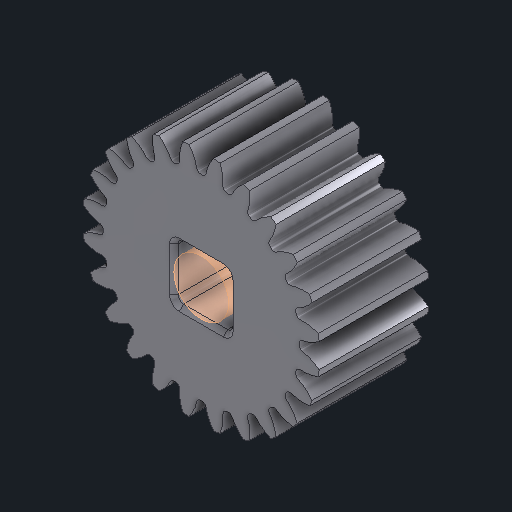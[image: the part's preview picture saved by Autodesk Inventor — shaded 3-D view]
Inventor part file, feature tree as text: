
AUTODESK INVENTOR PART (.ipt)
format: ipt  version: 2025 (Build 290162000, 162)  size: 466,944 bytes
history: native  units: in
note: dims shown in document units (in); Inventor stores cm internally (conversion verified against a paired STEP export)
features: other x5, sketch x1
ambient origin geometry x8: Origin, YZ Plane, XZ Plane, XY Plane, X Axis, Y Axis, Z Axis, Center Point
bodies: Solid1 (feature_tree)
feature tree (6):
  other  "HS 24T Gear, No Insert.ipt"
  other  "Solid1::HS 24T Gear, No Insert.ipt"
  other  "TaggingFeature1"
  sketch  "Sketch1"  dims[d0=0.3937in]
  other  "Srf1"
  other  "Srf1::Derived"
